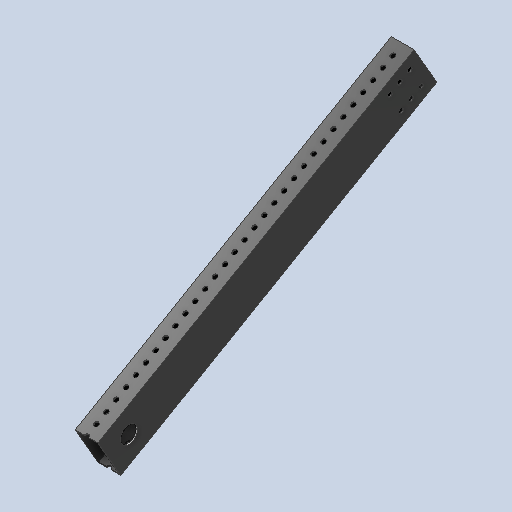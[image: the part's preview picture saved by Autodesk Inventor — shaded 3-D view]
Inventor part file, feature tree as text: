
AUTODESK INVENTOR PART (.ipt)
format: ipt  version: 2024 (Build 280153000, 153)  size: 270,848 bytes
history: native  units: in
note: dims shown in document units (in); Inventor stores cm internally (conversion verified against a paired STEP export)
features: other x4, extrude x2, sketch x2, projected_geometry x1
ambient origin geometry x8: Origin, YZ Plane, XZ Plane, XY Plane, X Axis, Y Axis, Z Axis, Center Point
bodies: Body1 (feature_tree)
feature tree (9):
  other  "2024-210-000-Angle-Shootaur.ipt"
  extrude  "Extrusion1"  Depth=0.3937in TaperAngle=0.0deg
  extrude  "Extrusion2"  Depth=1.0in
  other  "2024-210-002-Angle-Beam::2024-210-000-Angle-Shootaur.ipt"
  other  "TaggingFeature1"
  sketch  "Sketch1"  dims[d0=0.3937in d1=6.0in d2=0.0in]
  projected_geometry  "Projected Loop1"
  sketch  "Sketch2"  dims[d3=0.75in d4=1.0in d5=1.0in d6=4.625in d7=0.0in]
  other  "2024-210-002-Angle-Beam"
